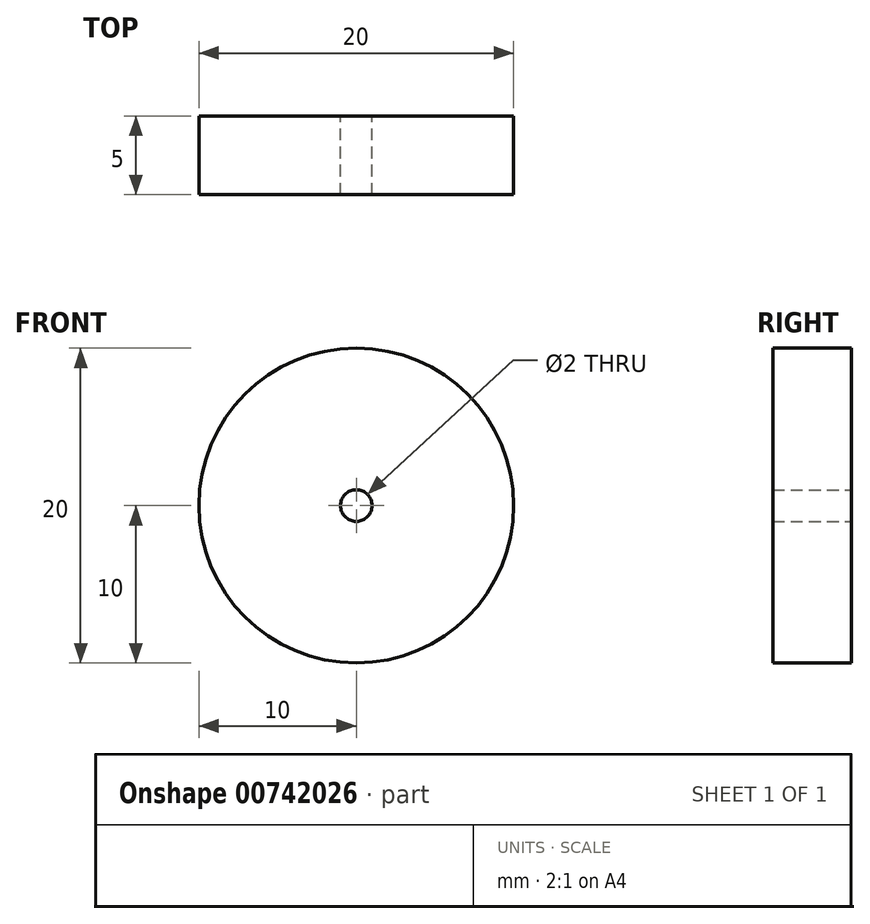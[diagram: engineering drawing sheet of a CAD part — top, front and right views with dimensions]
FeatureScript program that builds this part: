
annotation { "Feature Type Name" : "Feature", "Feature Type Description" : "" }
export const myFeature = defineFeature(function(context is Context, id is Id, definition is map)
    precondition{}
    {
        {
            var Q0;
            Q0=qCreatedBy(makeId("Front.planeOp"),FACE);
            var sketch = newSketch(context, id + "F0", { "sketchPlane" : qUnion([Q0])});
            skCircle(sketch, "E0", {"center": v(0, 0) * mm, "radius": 10 * mm});
            skCircle(sketch, "E1", {"center": v(0, 0) * mm, "radius": 1 * mm});
            skSolve(sketch);
        }
        {
            var Q0;
            Q0 = qSketchRegion(id + "F0", true);
            extrude(context, id + "F1", {"entities" : qUnion([Q0]), "depth" : 5 * mm, "offsetDistance" : 25 * mm});
        }
    });
